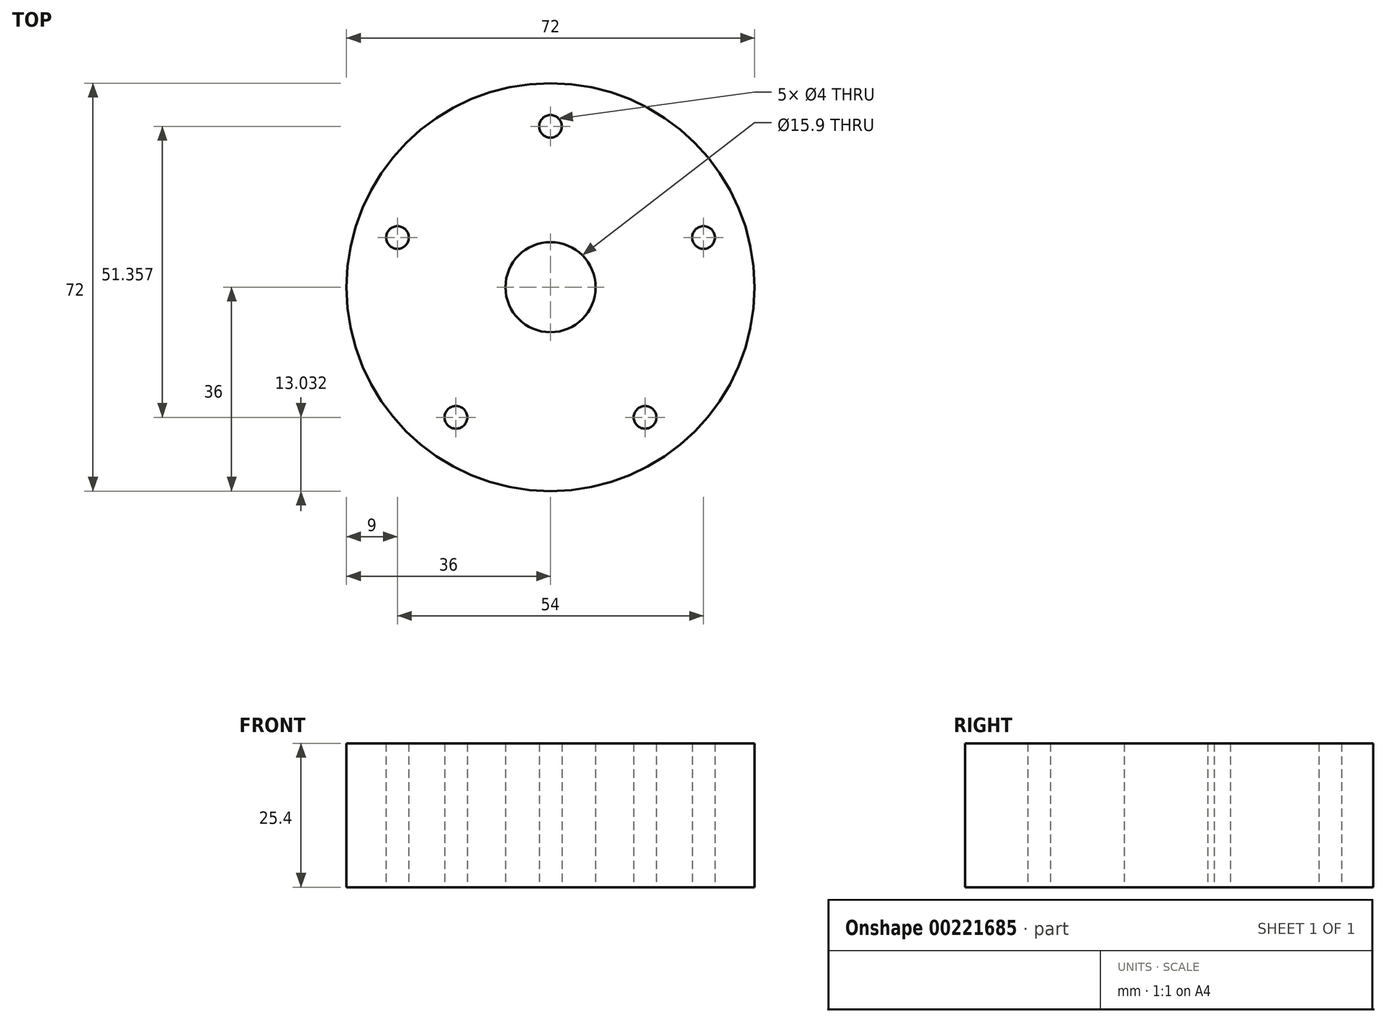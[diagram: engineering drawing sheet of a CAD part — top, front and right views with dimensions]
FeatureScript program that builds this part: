
annotation { "Feature Type Name" : "Feature", "Feature Type Description" : "" }
export const myFeature = defineFeature(function(context is Context, id is Id, definition is map)
    precondition{}
    {
        {
            var Q0;
            Q0=qCreatedBy(makeId("Top.planeOp"),FACE);
            var sketch = newSketch(context, id + "F0", { "sketchPlane" : qUnion([Q0])});
            skCircle(sketch, "E0", {"center": v(0, 28.39) * mm, "radius": 2 * mm});
            skCircle(sketch, "E1.1.0", {"center": v(-27, 8.77) * mm, "radius": 2 * mm});
            skCircle(sketch, "E1.2.0", {"center": v(-16.69, -22.97) * mm, "radius": 2 * mm});
            skCircle(sketch, "E1.3.0", {"center": v(16.69, -22.97) * mm, "radius": 2 * mm});
            skCircle(sketch, "E1.4.0", {"center": v(27, 8.77) * mm, "radius": 2 * mm});
            skPoint(sketch, "E1.center", {"position": v(0, 0) * mm});
            skCircle(sketch, "E2", {"center": v(0, 0) * mm, "radius": 36 * mm});
            skCircle(sketch, "E3", {"center": v(0, 0) * mm, "radius": 7.95 * mm});
            skSolve(sketch);
        }
        {
            var Q0;
            Q0 = qSketchRegion(id + "F0", true);
            extrude(context, id + "F1", {"entities" : qUnion([Q0]), "depth" : 25.4 * mm});
        }
    });
